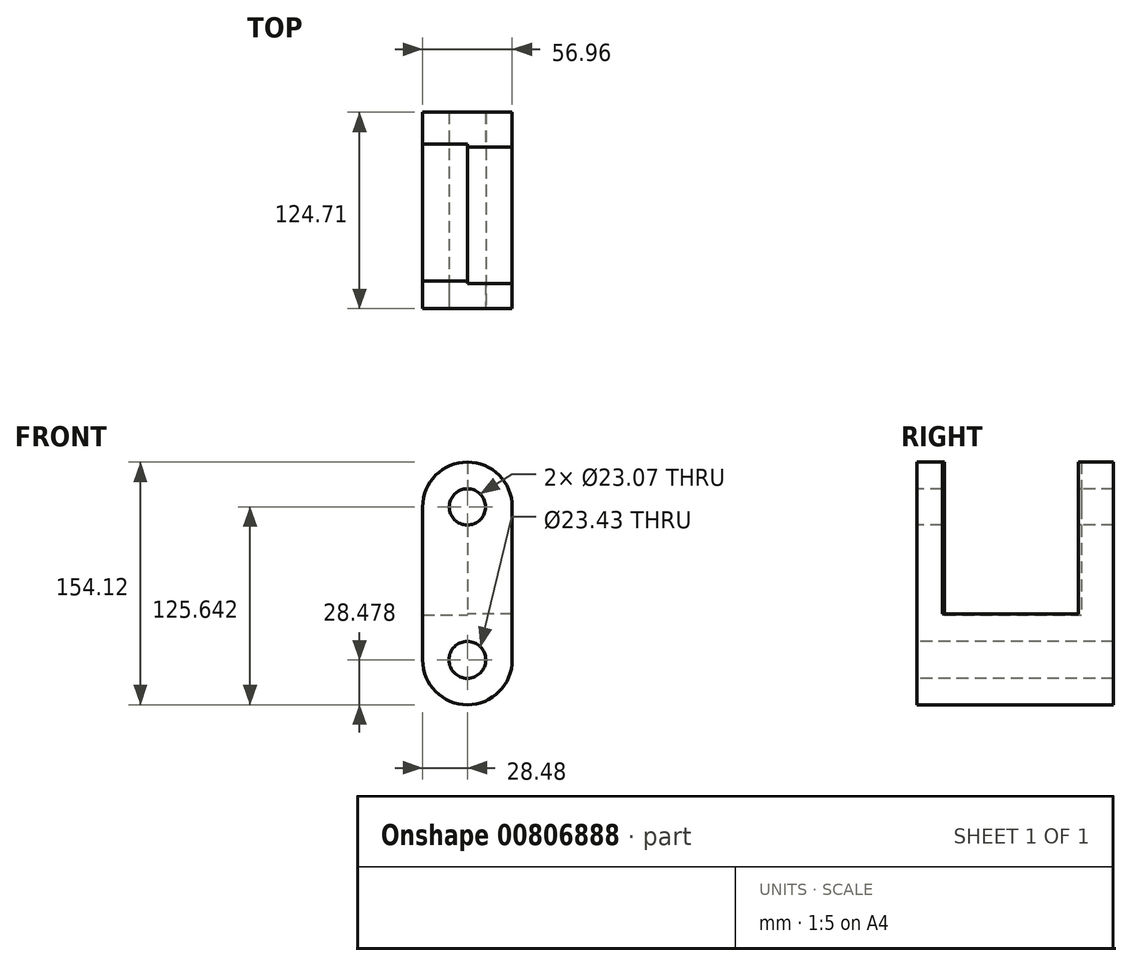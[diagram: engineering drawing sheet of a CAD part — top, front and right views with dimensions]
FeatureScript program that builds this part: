
annotation { "Feature Type Name" : "Feature", "Feature Type Description" : "" }
export const myFeature = defineFeature(function(context is Context, id is Id, definition is map)
    precondition{}
    {
        {
            var Q0;
            Q0=qCreatedBy(makeId("Front.planeOp"),FACE);
            var sketch = newSketch(context, id + "F0", { "sketchPlane" : qUnion([Q0])});
            skLineSegment(sketch, "E0.left", {"start": v(28.48, -48.58) * mm, "end": v(28.48, 48.58) * mm});
            skLineSegment(sketch, "E0.right", {"start": v(-28.48, -48.58) * mm, "end": v(-28.48, 48.58) * mm});
            skPoint(sketch, "E0.middle", {"position": v(0, 0) * mm});
            skArc(sketch, "E1", {"start": v(28.48, 48.58) * mm, "mid": v(0, 77.06) * mm, "end": v(-28.48, 48.58) * mm});
            skArc(sketch, "E2", {"start": v(-28.48, -48.58) * mm, "mid": v(0, -77.06) * mm, "end": v(28.48, -48.58) * mm});
            skCircle(sketch, "E3", {"center": v(0, 48.58) * mm, "radius": 11.54 * mm});
            skCircle(sketch, "E4", {"center": v(0, -48.58) * mm, "radius": 11.71 * mm});
            skSolve(sketch);
        }
        {
            var Q0;
            Q0=makeQuery(id+"F0.imprint","IMPRINT",FACE,{"disambiguationData":[TD([[makeQuery(id+"F0.imprint","IMPRINT",EDGE,{"derivedFrom":sQuery(id+"F0.wireOp",EDGE,"E0.left")}),1.0]])]});
            extrude(context, id + "F1", {"entities" : qUnion([Q0]), "oppositeDirection" : true, "depth" : 124.7 * mm, "offsetDistance" : 25.4 * mm});
        }
        {
            var Q0;
            Q0=qCreatedBy(makeId("Right.planeOp"),FACE);
            var sketch = newSketch(context, id + "F2", { "sketchPlane" : qUnion([Q0])});
            skLineSegment(sketch, "E5.bottom", {"start": v(17.41, 77.19) * mm, "end": v(104.43, 77.19) * mm});
            skLineSegment(sketch, "E5.top", {"start": v(17.41, -20.13) * mm, "end": v(104.43, -20.13) * mm});
            skLineSegment(sketch, "E5.left", {"start": v(17.41, 77.19) * mm, "end": v(17.41, -20.13) * mm});
            skLineSegment(sketch, "E5.right", {"start": v(104.43, 77.19) * mm, "end": v(104.43, -20.13) * mm});
            skSolve(sketch);
        }
        {
            var Q0;
            Q0 = qSketchRegion(id + "F2", true);
            extrude(context, id + "F3", {"entities" : qUnion([Q0]), "operationType" : NewBodyOperationType.REMOVE, "endBound" : BoundingType.THROUGH_ALL, "oppositeDirection" : true, "depth" : 25.4 * mm, "offsetDistance" : 25.4 * mm});
        }
        {
            var Q0;
            Q0=qCreatedBy(makeId("Right.planeOp"),FACE);
            var sketch = newSketch(context, id + "F4", { "sketchPlane" : qUnion([Q0])});
            skLineSegment(sketch, "E6.bottom", {"start": v(102.7, 77.73) * mm, "end": v(16.06, 77.73) * mm});
            skLineSegment(sketch, "E6.top", {"start": v(102.7, -19.4) * mm, "end": v(16.06, -19.4) * mm});
            skLineSegment(sketch, "E6.left", {"start": v(102.7, 77.73) * mm, "end": v(102.7, -19.4) * mm});
            skLineSegment(sketch, "E6.right", {"start": v(16.06, 77.73) * mm, "end": v(16.06, -19.4) * mm});
            skSolve(sketch);
        }
        {
            var Q0;
            Q0 = qSketchRegion(id + "F4", true);
            extrude(context, id + "F5", {"entities" : qUnion([Q0]), "operationType" : NewBodyOperationType.REMOVE, "endBound" : BoundingType.THROUGH_ALL, "depth" : 25.4 * mm, "offsetDistance" : 25.4 * mm});
        }
    });
